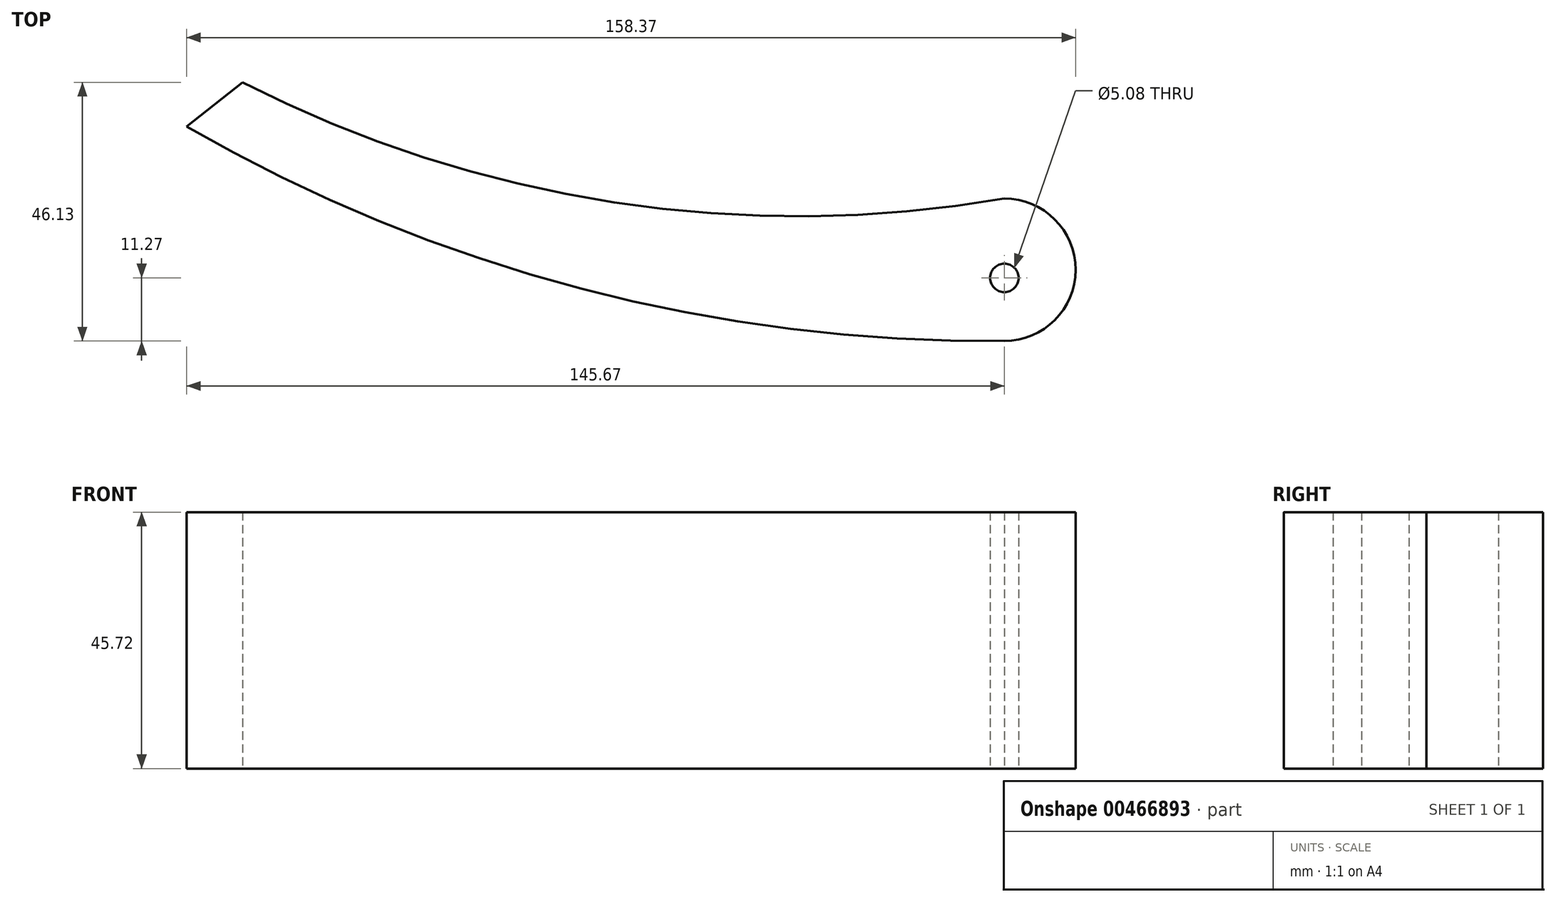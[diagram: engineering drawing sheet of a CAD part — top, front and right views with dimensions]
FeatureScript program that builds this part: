
annotation { "Feature Type Name" : "Feature", "Feature Type Description" : "" }
export const myFeature = defineFeature(function(context is Context, id is Id, definition is map)
    precondition{}
    {
        {
            var Q0;
            Q0=qCreatedBy(makeId("Top.planeOp"),FACE);
            var sketch = newSketch(context, id + "F0", { "sketchPlane" : qUnion([Q0])});
            skArc(sketch, "E0", {"start": v(0, -11.26) * mm, "mid": v(12.7, 1.44) * mm, "end": v(0, 14.14) * mm});
            skArc(sketch, "E1", {"start": v(-145.67, 26.96) * mm, "mid": v(-75.4, -1.92) * mm, "end": v(0, -11.26) * mm});
            skArc(sketch, "E2", {"start": v(-135.72, 34.86) * mm, "mid": v(-69.55, 13.47) * mm, "end": v(0, 14.14) * mm});
            skLineSegment(sketch, "E3", {"start": v(-145.67, 26.96) * mm, "end": v(-135.72, 34.86) * mm});
            skSolve(sketch);
        }
        {
            var Q0;
            Q0=makeQuery(id+"F0.imprint","IMPRINT",FACE,{"disambiguationData":[TD([[makeQuery(id+"F0.imprint","IMPRINT",EDGE,{"derivedFrom":sQuery(id+"F0.wireOp",EDGE,"E0")}),1.0]])]});
            extrude(context, id + "F1", {"entities" : qUnion([Q0]), "depth" : 45.72 * mm});
        }
        {
            var Q0;
            Q0=qCreatedBy(makeId("Top.planeOp"),FACE);
            var sketch = newSketch(context, id + "F2", { "sketchPlane" : qUnion([Q0])});
            skCircle(sketch, "E4", {"center": v(0, 0) * mm, "radius": 2.54 * mm});
            skSolve(sketch);
        }
        {
            var Q0;
            Q0=makeQuery(id+"F2.imprint","IMPRINT",FACE,{"disambiguationData":[TD([[makeQuery(id+"F2.imprint","IMPRINT",EDGE,{"derivedFrom":sQuery(id+"F2.wireOp",EDGE,"E4")}),1.0]])]});
            extrude(context, id + "F3", {"entities" : qUnion([Q0]), "operationType" : NewBodyOperationType.REMOVE, "endBound" : BoundingType.THROUGH_ALL, "depth" : 25.4 * mm});
        }
    });
